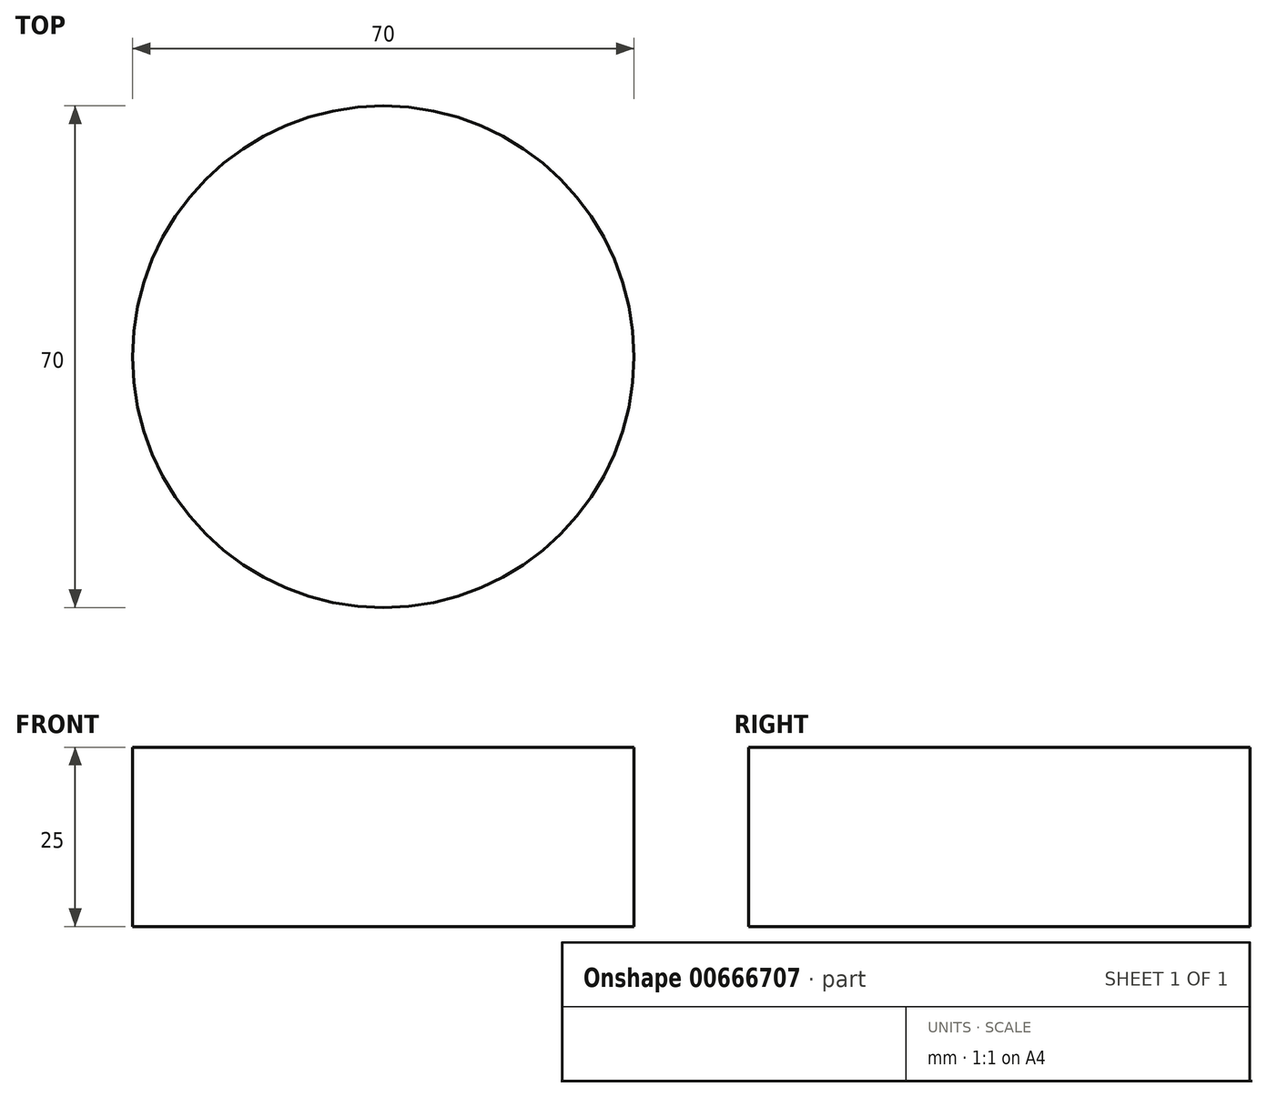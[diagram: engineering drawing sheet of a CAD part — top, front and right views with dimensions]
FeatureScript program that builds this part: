
annotation { "Feature Type Name" : "Feature", "Feature Type Description" : "" }
export const myFeature = defineFeature(function(context is Context, id is Id, definition is map)
    precondition{}
    {
        {
            var Q0;
            Q0=qCreatedBy(makeId("Right.planeOp"),FACE);
            var sketch = newSketch(context, id + "F0", { "sketchPlane" : qUnion([Q0])});
            skLineSegment(sketch, "E0.bottom", {"start": v(0, 33.24) * mm, "end": v(35, 33.24) * mm});
            skLineSegment(sketch, "E0.top", {"start": v(0, 8.24) * mm, "end": v(35, 8.24) * mm});
            skLineSegment(sketch, "E0.left", {"start": v(0, 33.24) * mm, "end": v(0, 8.24) * mm});
            skLineSegment(sketch, "E0.right", {"start": v(35, 33.24) * mm, "end": v(35, 8.24) * mm});
            skLineSegment(sketch, "E1", {"start": v(0, 58.67) * mm, "end": v(0, -16.44) * mm, "construction": true});
            skSolve(sketch);
        }
        {
            var Q0;
            Q0=makeQuery(id+"F0.imprint","IMPRINT",FACE,{"disambiguationData":[TD([[makeQuery(id+"F0.imprint","IMPRINT",EDGE,{"derivedFrom":sQuery(id+"F0.wireOp",EDGE,"E0.bottom")}),-1.0]])]});
            var Q1;
            Q1=sQuery(id+"F0.wireOp",EDGE,"E1");
            revolve(context, id + "F1", {"entities" : qUnion([Q0]), "axis" : qUnion([Q1]), "revolveType" : RevolveType.FULL});
        }
    });
